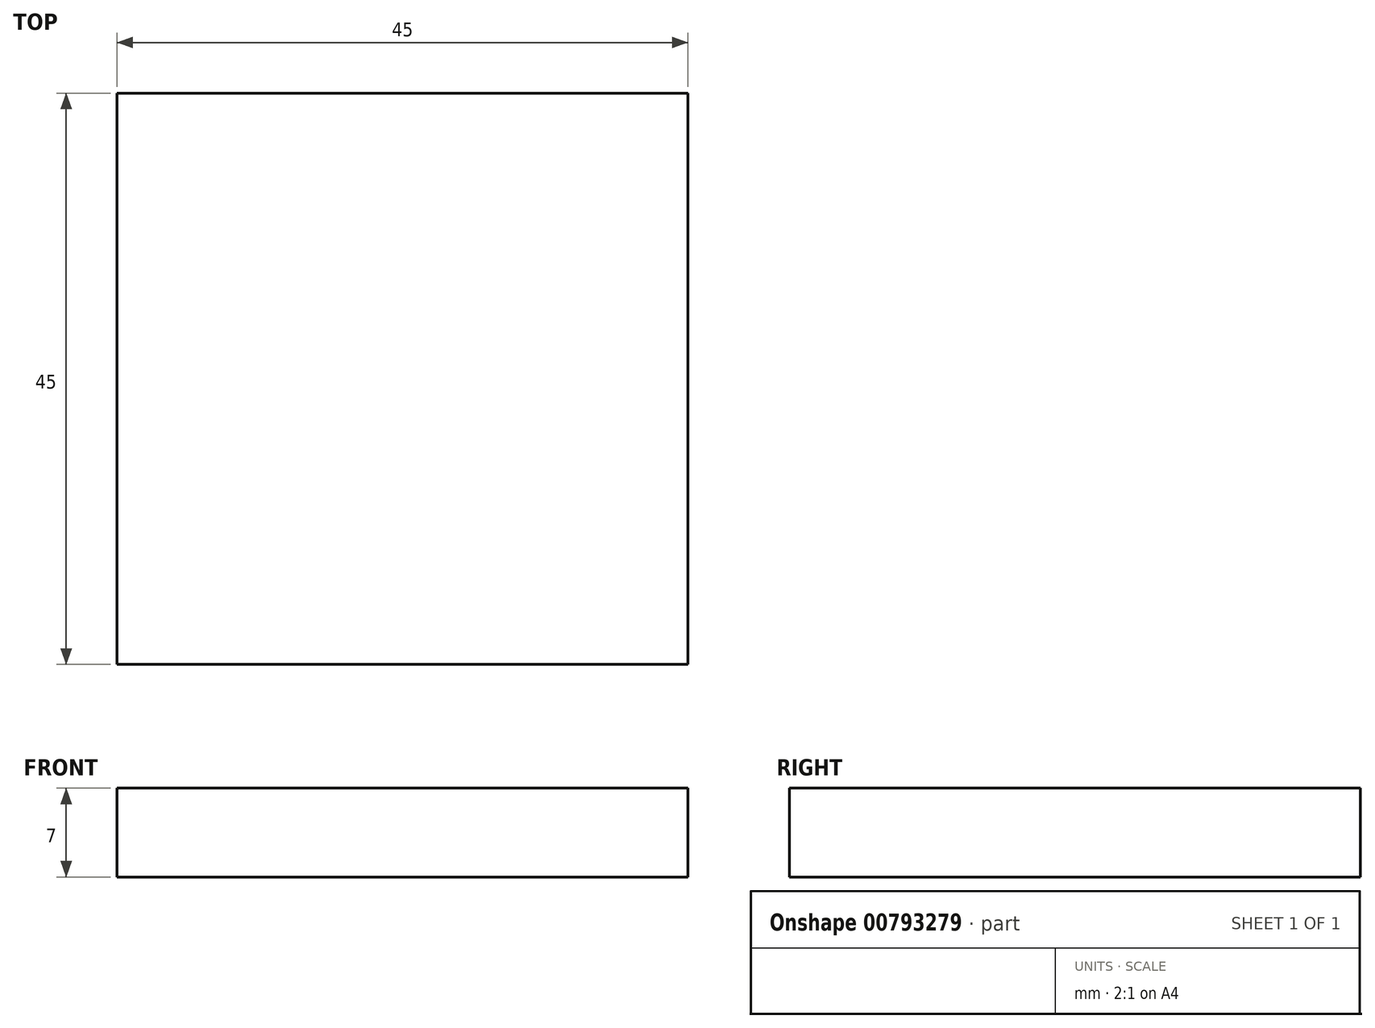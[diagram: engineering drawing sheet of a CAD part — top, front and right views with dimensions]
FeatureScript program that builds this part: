
annotation { "Feature Type Name" : "Feature", "Feature Type Description" : "" }
export const myFeature = defineFeature(function(context is Context, id is Id, definition is map)
    precondition{}
    {
        {
            var Q0;
            Q0=qCreatedBy(makeId("Top.planeOp"),FACE);
            var sketch = newSketch(context, id + "F0", { "sketchPlane" : qUnion([Q0])});
            skLineSegment(sketch, "E0.bottom", {"start": v(22.5, 22.5) * mm, "end": v(-22.5, 22.5) * mm});
            skLineSegment(sketch, "E0.top", {"start": v(22.5, -22.5) * mm, "end": v(-22.5, -22.5) * mm});
            skLineSegment(sketch, "E0.left", {"start": v(22.5, 22.5) * mm, "end": v(22.5, -22.5) * mm});
            skLineSegment(sketch, "E0.right", {"start": v(-22.5, 22.5) * mm, "end": v(-22.5, -22.5) * mm});
            skPoint(sketch, "E0.middle", {"position": v(0, 0) * mm});
            skSolve(sketch);
        }
        {
            var Q0;
            Q0=makeQuery(id+"F0.imprint","IMPRINT",FACE,{"disambiguationData":[TD([[makeQuery(id+"F0.imprint","IMPRINT",EDGE,{"derivedFrom":sQuery(id+"F0.wireOp",EDGE,"E0.bottom")}),1.0]])]});
            extrude(context, id + "F1", {"entities" : qUnion([Q0]), "depth" : 7 * mm, "offsetDistance" : 25 * mm});
        }
    });
